FCSTD DOCUMENT  (FreeCAD 1.0R39319 (Git))
Label: Cable_y_minus-CrossSection
License: All rights reserved
LicenseURL: https://en.wikipedia.org/wiki/All_rights_reserved
objects: App::DocumentObjectGroupPython×3, App::FeaturePython×1, Part::Part2DObjectPython×1, App::DocumentObjectGroup×1
note: 1 computed .brp shape members not serialized (recipe doc carries the construction recipe); baked Part::Feature solids carry a one-line shape summary decoded from their .brp

FEATURE [App::FeaturePython] PECMaterial  label="PEC"  # WARN: FeaturePython — macro-defined, semantics opaque (R4)
FEATURE [Part::Part2DObjectPython] Circle003  label="Conductor"  # Draft 2D object (typed FeaturePython)
  Area = 3.14159
  FirstAngle = 0
  LastAngle = 0
  MakeFace = true
  Material = -> PECMaterial
  Placement = pos=(20,0,0) rot=(0,0,1;0rad)
  Radius = 1
FEATURE [App::DocumentObjectGroupPython] MaterialGroup  label="Materials"  # scripted group (container) (typed FeaturePython)
  Group = -> [PECMaterial]
FEATURE [App::DocumentObjectGroup] Group  label="Conductors"
  Group = -> [Circle003]
FEATURE [App::DocumentObjectGroupPython] CaseStudy  label="Model"  # scripted group (container) (typed FeaturePython)
  Group = -> [Group]
FEATURE [App::DocumentObjectGroupPython] CrossSection  label="Cross-Section"  # scripted group (container) (typed FeaturePython)
  Group = -> [MaterialGroup,CaseStudy]
